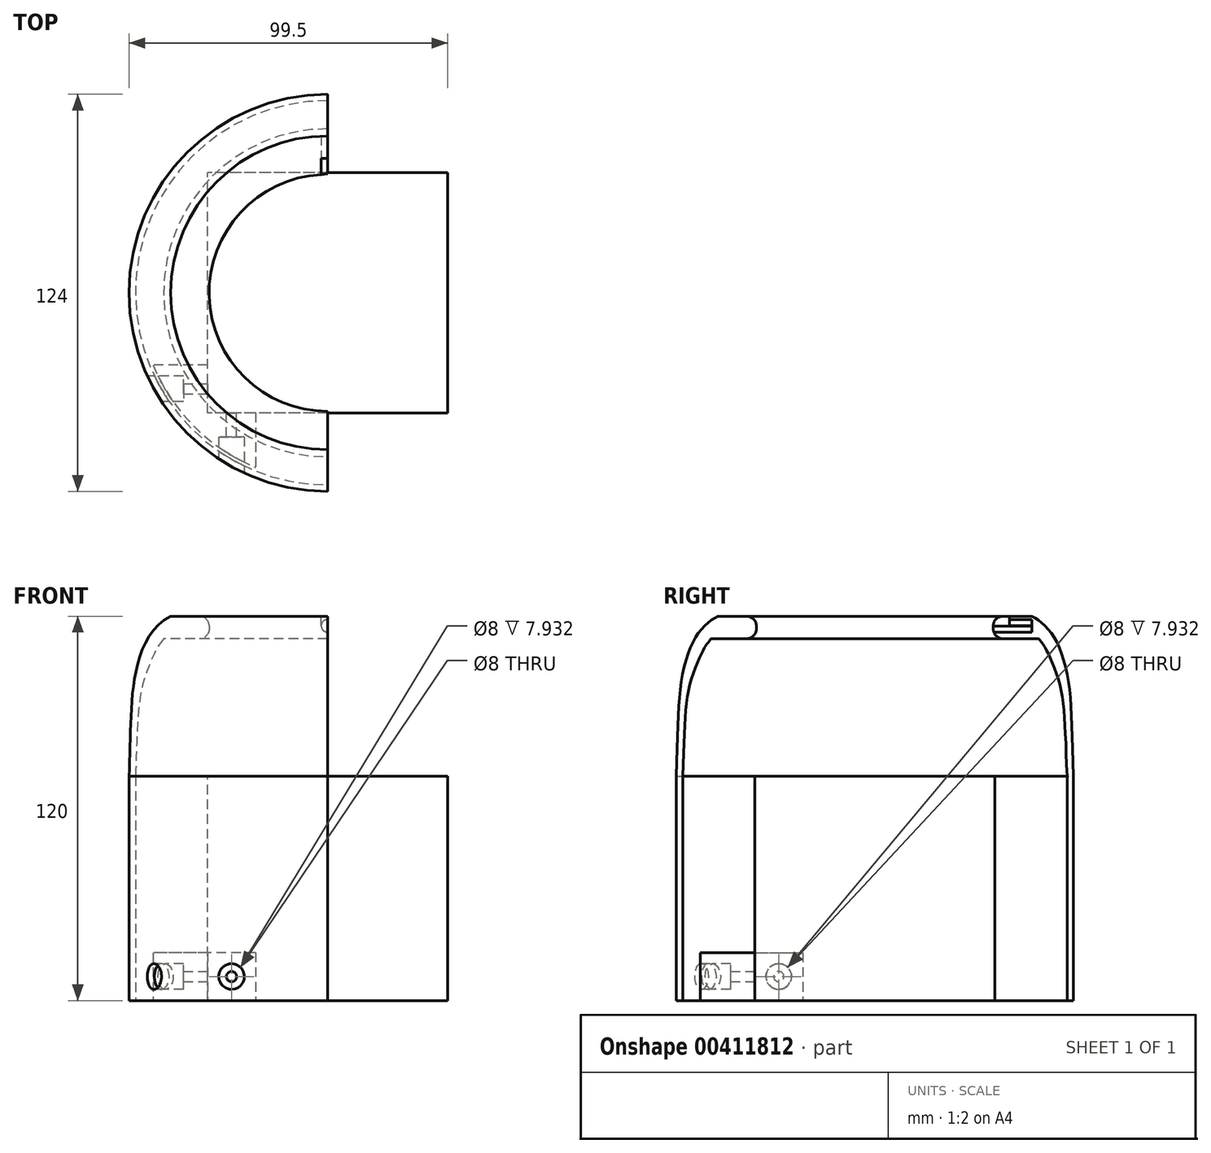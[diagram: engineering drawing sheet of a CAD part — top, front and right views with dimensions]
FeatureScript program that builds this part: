
annotation { "Feature Type Name" : "Feature", "Feature Type Description" : "" }
export const myFeature = defineFeature(function(context is Context, id is Id, definition is map)
    precondition{}
    {
        {
            var Q0;
            Q0=qCreatedBy(makeId("Front.planeOp"),FACE);
            var sketch = newSketch(context, id + "F0", { "sketchPlane" : qUnion([Q0])});
            skLineSegment(sketch, "E0", {"start": v(-40, 50) * mm, "end": v(-49, 50) * mm});
            skLineSegment(sketch, "E1", {"start": v(-62, 0) * mm, "end": v(-62, -70) * mm});
            skLineSegment(sketch, "E2", {"start": v(-37, 47) * mm, "end": v(-37, 46) * mm});
            skLineSegment(sketch, "E3", {"start": v(-40, 43) * mm, "end": v(-51.2, 43) * mm});
            skFitSpline(sketch, "E4", {"points": [v(-49, 50) * mm, v(-52.64, 47.47) * mm, v(-56.76, 41.98) * mm, v(-60.39, 29.9) * mm, v(-62, 0) * mm], "startDerivative": vector(-21.37, -10.6) * mm, "endDerivative": vector(-3.86, -109.3) * mm});
            skPoint(sketch, "E5.visualSharp", {"position": v(-37, 50) * mm});
            skArc(sketch, "E5.filletArc", {"start": v(-37, 47) * mm, "mid": v(-37.88, 49.12) * mm, "end": v(-40, 50) * mm});
            skPoint(sketch, "E6.visualSharp", {"position": v(-37, 43) * mm});
            skArc(sketch, "E6.filletArc", {"start": v(-40, 43) * mm, "mid": v(-37.88, 43.88) * mm, "end": v(-37, 46) * mm});
            skFitSpline(sketch, "E7", {"points": [v(-51.2, 43) * mm, v(-53.22, 40.09) * mm, v(-57.32, 30.2) * mm, v(-60, 0) * mm], "startDerivative": vector(-23.74, -33.12) * mm, "endDerivative": vector(-3.58, -89.87) * mm});
            skLineSegment(sketch, "E8", {"start": v(-62, -70) * mm, "end": v(0, -70) * mm});
            skLineSegment(sketch, "E9", {"start": v(0, -70) * mm, "end": v(0, -69.08) * mm});
            skLineSegment(sketch, "E10", {"start": v(-60, 0) * mm, "end": v(-60, -70) * mm});
            skSolve(sketch);
        }
        {
            var Q0;
            Q0=makeQuery(id+"F0.imprint","IMPRINT",FACE,{"disambiguationData":[TD([[makeQuery(id+"F0.imprint","IMPRINT",EDGE,{"derivedFrom":sQuery(id+"F0.wireOp",EDGE,"E0")}),1.0]])]});
            var Q1;
            Q1=sQuery(id+"F0.wireOp",EDGE,"E9");
            revolve(context, id + "F1", {"entities" : qUnion([Q0]), "axis" : qUnion([Q1]), "revolveType" : RevolveType.SYMMETRIC, "angle" : 180 * degree});
        }
        {
            var Q0;
            Q0=qCreatedBy(makeId("Front.planeOp"),FACE);
            var sketch = newSketch(context, id + "F2", { "sketchPlane" : qUnion([Q0])});
            skCircle(sketch, "E11", {"center": v(0, 47) * mm, "radius": 2 * mm});
            skLineSegment(sketch, "E12", {"start": v(-2, 47.07) * mm, "end": v(-2, 42.07) * mm});
            skLineSegment(sketch, "E13", {"start": v(-2, 42.07) * mm, "end": v(0, 42.07) * mm});
            skLineSegment(sketch, "E14", {"start": v(0, 42.07) * mm, "end": v(0, 45) * mm});
            skLineSegment(sketch, "E15", {"start": v(-2, 47.07) * mm, "end": v(-2, 50.36) * mm});
            skLineSegment(sketch, "E16", {"start": v(0, 50.36) * mm, "end": v(0, 49) * mm});
            skLineSegment(sketch, "E17", {"start": v(-2, 50.36) * mm, "end": v(0, 50.36) * mm});
            skSolve(sketch);
        }
        {
            var Q0;
            {var subQ1=sQuery(id+"F2.wireOp",EDGE,"E11");var subQ4=makeQuery(id+"F2.imprint","INTERSECT",VERTEX,{"derivedFrom":[subQ1,sQuery(id+"F2.wireOp",EDGE,"E14")]});Q0=makeQuery(id+"F2.imprint","IMPRINT",FACE,{"disambiguationData":[TD([[makeQuery(id+"F2.imprint","IMPRINT",EDGE,{"disambiguationData":[TD([[subQ4,1.0]])],"derivedFrom":subQ1}),1.0]])]});}
            extrude(context, id + "F3", {"entities" : qUnion([Q0]), "operationType" : NewBodyOperationType.REMOVE, "oppositeDirection" : true, "depth" : 49 * mm});
        }
        {
            var Q0;
            {var subQ0=sQuery(id+"F2.wireOp",EDGE,"E15");Q0=makeQuery(id+"F2.imprint","IMPRINT",FACE,{"disambiguationData":[TD([[makeQuery(id+"F2.imprint","IMPRINT",EDGE,{"derivedFrom":subQ0}),-1.0]])]});}
            extrude(context, id + "F4", {"entities" : qUnion([Q0]), "operationType" : NewBodyOperationType.REMOVE, "oppositeDirection" : true, "depth" : 42 * mm});
        }
        {
            var Q0;
            Q0=qCreatedBy(makeId("Top.planeOp"),FACE);
            var sketch = newSketch(context, id + "F5", { "sketchPlane" : qUnion([Q0])});
            skLineSegment(sketch, "E18.bottom", {"start": v(37.5, -37.5) * mm, "end": v(-37.5, -37.5) * mm});
            skLineSegment(sketch, "E18.top", {"start": v(37.5, 37.5) * mm, "end": v(-37.5, 37.5) * mm});
            skLineSegment(sketch, "E18.left", {"start": v(37.5, -37.5) * mm, "end": v(37.5, 37.5) * mm});
            skLineSegment(sketch, "E18.right", {"start": v(-37.5, -37.5) * mm, "end": v(-37.5, 37.5) * mm});
            skSolve(sketch);
        }
        {
            var Q0;
            Q0=makeQuery(id+"F5.imprint","IMPRINT",FACE,{"disambiguationData":[TD([[makeQuery(id+"F5.imprint","IMPRINT",EDGE,{"derivedFrom":sQuery(id+"F5.wireOp",EDGE,"E18.bottom")}),-1.0]])]});
            extrude(context, id + "F6", {"entities" : qUnion([Q0]), "operationType" : NewBodyOperationType.ADD, "oppositeDirection" : true, "depth" : 70 * mm});
        }
        {
            var Q0;
            Q0=makeQuery(id+"F6.opExtrude","CAP_FACE",FACE,{"disambiguationData":[OSD([sQuery(id+"F5.wireOp",EDGE,"E18.bottom"),sQuery(id+"F5.wireOp",EDGE,"E18.top"),sQuery(id+"F5.wireOp",EDGE,"E18.left"),sQuery(id+"F5.wireOp",EDGE,"E18.right")])],"isStart":false});
            var sketch = newSketch(context, id + "F7", { "sketchPlane" : qUnion([Q0])});
            skLineSegment(sketch, "E19", {"start": v(-37.5, 37.5) * mm, "end": v(-37.5, 22.5) * mm});
            skLineSegment(sketch, "E20", {"start": v(-37.5, 22.5) * mm, "end": v(-54.5, 22.5) * mm});
            skLineSegment(sketch, "E21", {"start": v(-37.5, 37.5) * mm, "end": v(-22.5, 37.5) * mm});
            skLineSegment(sketch, "E22", {"start": v(-22.5, 37.5) * mm, "end": v(-22.5, 54.5) * mm});
            skArc(sketch, "E23", {"start": v(-22.5, 54.5) * mm, "mid": v(-41.71, 41.71) * mm, "end": v(-54.5, 22.5) * mm});
            skSolve(sketch);
        }
        {
            var Q0;
            Q0=makeQuery(id+"F7.imprint","IMPRINT",FACE,{"disambiguationData":[TD([[makeQuery(id+"F7.imprint","IMPRINT",EDGE,{"derivedFrom":sQuery(id+"F7.wireOp",EDGE,"E19")}),-1.0]])]});
            extrude(context, id + "F8", {"entities" : qUnion([Q0]), "oppositeDirection" : true, "depth" : 15 * mm});
        }
        {
            var Q0;
            Q0=makeQuery(id+"F8.opExtrude","SWEPT_FACE",FACE,{"disambiguationData":[OSD([sQuery(id+"F7.wireOp",EDGE,"E19")])]});
            var sketch = newSketch(context, id + "F9", { "sketchPlane" : qUnion([Q0])});
            skCircle(sketch, "E24", {"center": v(-30, -62.5) * mm, "radius": 1.6 * mm});
            skSolve(sketch);
        }
        {
            var Q0;
            Q0=makeQuery(id+"F9.imprint","IMPRINT",FACE,{"disambiguationData":[TD([[makeQuery(id+"F9.imprint","IMPRINT",EDGE,{"derivedFrom":sQuery(id+"F9.wireOp",EDGE,"E24")}),1.0]])]});
            extrude(context, id + "F10", {"entities" : qUnion([Q0]), "operationType" : NewBodyOperationType.REMOVE, "oppositeDirection" : true, "depth" : 15 * mm});
        }
        {
            var Q0;
            Q0=qCreatedBy(makeId("Right.planeOp"),FACE);
            cPlane(context, id + "F11", {"entities" : qUnion([Q0]), "cplaneType" : CPlaneType.OFFSET, "offset" : 60 * mm, "oppositeDirection" : true, "width" : 150 * mm, "height" : 150 * mm});
        }
        {
            var Q0;
            Q0=qCreatedBy(id+"F11.planeOp",FACE);
            var sketch = newSketch(context, id + "F12", { "sketchPlane" : qUnion([Q0])});
            skCircle(sketch, "E25", {"center": v(-30, -62.5) * mm, "radius": 4 * mm});
            skSolve(sketch);
        }
        {
            var Q0;
            Q0=qSketchRegion(id+"F12",true);
            extrude(context, id + "F13", {"entities" : qUnion([Q0]), "operationType" : NewBodyOperationType.REMOVE, "depth" : 15 * mm});
        }
        {
            var Q0;
            Q0=makeQuery(id+"F8.opExtrude","SWEPT_FACE",FACE,{"disambiguationData":[OSD([sQuery(id+"F7.wireOp",EDGE,"E21")])]});
            var sketch = newSketch(context, id + "F14", { "sketchPlane" : qUnion([Q0])});
            skCircle(sketch, "E26", {"center": v(30, -62.5) * mm, "radius": 1.6 * mm});
            skSolve(sketch);
        }
        {
            var Q0;
            Q0=makeQuery(id+"F14.imprint","IMPRINT",FACE,{"disambiguationData":[TD([[makeQuery(id+"F14.imprint","IMPRINT",EDGE,{"derivedFrom":sQuery(id+"F14.wireOp",EDGE,"E26")}),1.0]])]});
            extrude(context, id + "F15", {"entities" : qUnion([Q0]), "operationType" : NewBodyOperationType.REMOVE, "oppositeDirection" : true, "depth" : 15 * mm});
        }
        {
            var Q0;
            Q0=qCreatedBy(makeId("Front.planeOp"),FACE);
            cPlane(context, id + "F16", {"entities" : qUnion([Q0]), "cplaneType" : CPlaneType.OFFSET, "offset" : 60 * mm, "width" : 150 * mm, "height" : 150 * mm});
        }
        {
            var Q0;
            Q0=qCreatedBy(id+"F16.planeOp",FACE);
            var sketch = newSketch(context, id + "F17", { "sketchPlane" : qUnion([Q0])});
            skCircle(sketch, "E27", {"center": v(-30, -62.5) * mm, "radius": 4 * mm});
            skSolve(sketch);
        }
        {
            var Q0;
            Q0=qSketchRegion(id+"F17",true);
            extrude(context, id + "F18", {"entities" : qUnion([Q0]), "operationType" : NewBodyOperationType.REMOVE, "oppositeDirection" : true, "depth" : 15 * mm});
        }
    });
